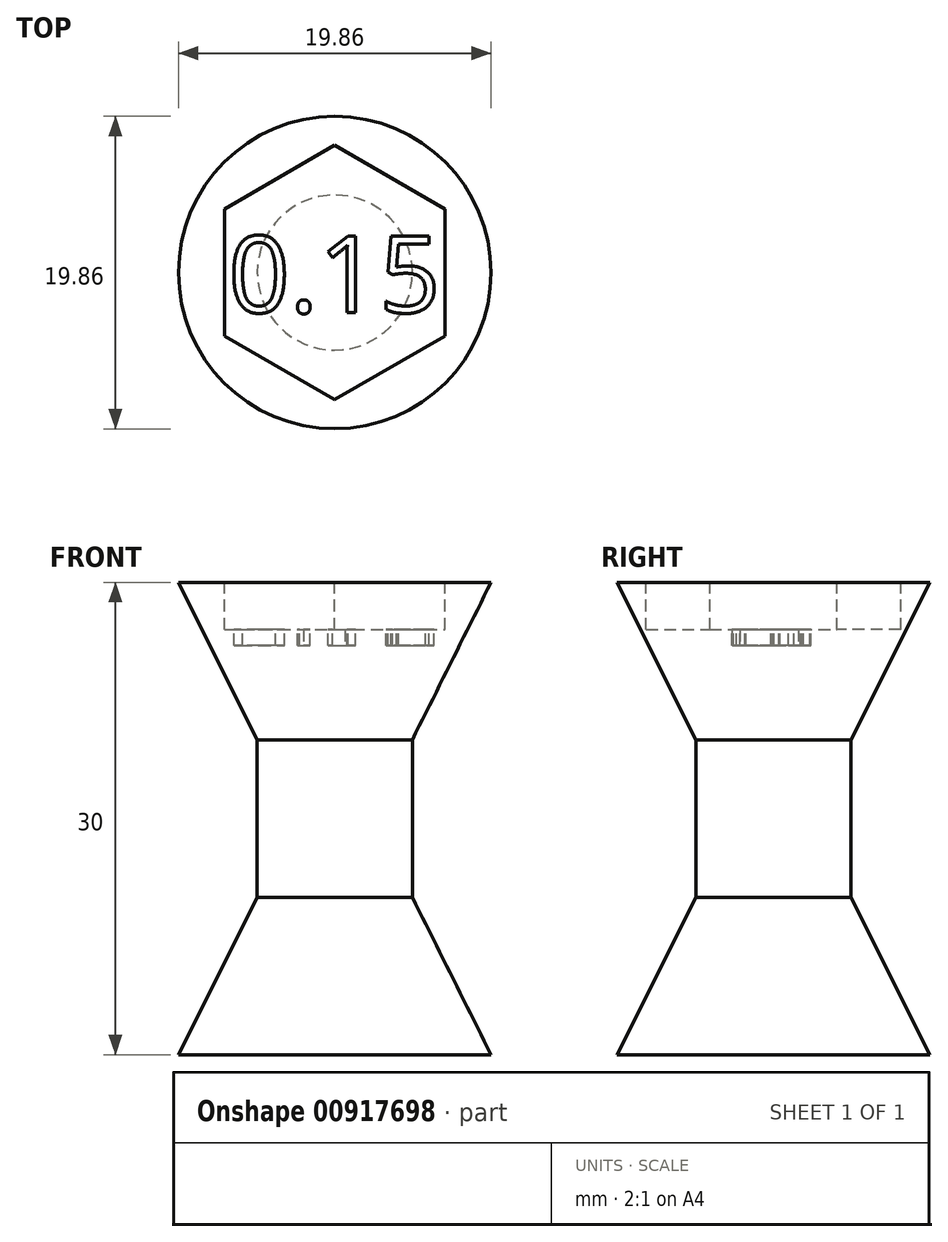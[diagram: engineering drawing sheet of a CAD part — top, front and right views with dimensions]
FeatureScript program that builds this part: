
annotation { "Feature Type Name" : "Feature", "Feature Type Description" : "" }
export const myFeature = defineFeature(function(context is Context, id is Id, definition is map)
    precondition{}
    {
        {
            var Q0;
            Q0=qCreatedBy(makeId("Front.planeOp"),FACE);
            var sketch = newSketch(context, id + "F0", { "sketchPlane" : qUnion([Q0])});
            skLineSegment(sketch, "E0", {"start": v(0, 15) * mm, "end": v(0, -15) * mm});
            skLineSegment(sketch, "E1", {"start": v(0, -15) * mm, "end": v(9.93, -15) * mm});
            skLineSegment(sketch, "E2", {"start": v(9.93, -15) * mm, "end": v(4.92, -5) * mm});
            skLineSegment(sketch, "E3", {"start": v(4.92, -5) * mm, "end": v(4.92, 5) * mm});
            skLineSegment(sketch, "E4", {"start": v(4.92, 5) * mm, "end": v(9.92, 15) * mm});
            skLineSegment(sketch, "E5", {"start": v(9.92, 15) * mm, "end": v(0, 15) * mm});
            skSolve(sketch);
        }
        {
            var Q0;
            Q0=makeQuery(id+"F0.imprint","IMPRINT",FACE,{"disambiguationData":[TD([[makeQuery(id+"F0.imprint","IMPRINT",EDGE,{"derivedFrom":sQuery(id+"F0.wireOp",EDGE,"E0")}),1.0]])]});
            var Q1;
            Q1=sQuery(id+"F0.wireOp",EDGE,"E0");
            var Q2;
            Q2=sQuery(id+"F0.wireOp",EDGE,"E1");
            var Q3;
            Q3=sQuery(id+"F0.wireOp",EDGE,"E2");
            var Q4;
            Q4=sQuery(id+"F0.wireOp",EDGE,"E3");
            var Q5;
            Q5=sQuery(id+"F0.wireOp",EDGE,"E4");
            var Q6;
            Q6=sQuery(id+"F0.wireOp",EDGE,"E5");
            var Q7;
            Q7=sQuery(id+"F0.wireOp",EDGE,"E0");
            revolve(context, id + "F1", {"surfaceOperationType" : NewSurfaceOperationType.ADD, "entities" : qUnion([Q0]), "surfaceEntities" : qUnion([Q1, Q2, Q3, Q4, Q5, Q6]), "axis" : qUnion([Q7]), "revolveType" : RevolveType.FULL});
        }
        {
            var Q0;
            Q0=makeQuery(id+"F1.opRevolve","SWEPT_FACE",FACE,{"disambiguationData":[OSD([sQuery(id+"F0.wireOp",EDGE,"E5")])]});
            var sketch = newSketch(context, id + "F2", { "sketchPlane" : qUnion([Q0])});
            skCircle(sketch, "E6.cCircle", {"center": v(0, 0) * mm, "radius": 7 * mm, "construction": true});
            skLineSegment(sketch, "E6.0", {"start": v(0, 8.08) * mm, "end": v(7, 4.04) * mm});
            skLineSegment(sketch, "E6.1", {"start": v(7, 4.04) * mm, "end": v(7, -4.04) * mm});
            skLineSegment(sketch, "E6.2", {"start": v(7, -4.04) * mm, "end": v(0, -8.08) * mm});
            skLineSegment(sketch, "E6.3", {"start": v(0, -8.08) * mm, "end": v(-7, -4.04) * mm});
            skLineSegment(sketch, "E6.4", {"start": v(-7, -4.04) * mm, "end": v(-7, 4.04) * mm});
            skLineSegment(sketch, "E6.5", {"start": v(-7, 4.04) * mm, "end": v(0, 8.08) * mm});
            skPoint(sketch, "E6.0.midPoint", {"position": v(3.5, 6.06) * mm});
            skSolve(sketch);
        }
        {
            var Q0;
            Q0 = qSketchRegion(id + "F2", true);
            extrude(context, id + "F3", {"entities" : qUnion([Q0]), "operationType" : NewBodyOperationType.REMOVE, "oppositeDirection" : true, "depth" : 3 * mm, "offsetDistance" : 25 * mm});
        }
        {
            var Q0;
            Q0=makeQuery(id+"F3.boolean.opBoolean","COPY",FACE,{"derivedFrom":makeQuery(id+"F3.opExtrude","CAP_FACE",FACE,{"disambiguationData":[OSD([sQuery(id+"F2.wireOp",EDGE,"E6.0"),sQuery(id+"F2.wireOp",EDGE,"E6.1"),sQuery(id+"F2.wireOp",EDGE,"E6.2"),sQuery(id+"F2.wireOp",EDGE,"E6.3"),sQuery(id+"F2.wireOp",EDGE,"E6.4"),sQuery(id+"F2.wireOp",EDGE,"E6.5")])],"isStart":false})});
            var sketch = newSketch(context, id + "F4", { "sketchPlane" : qUnion([Q0])});
            skText(sketch, "E7", { "text": "0.15", "fontName": "OpenSans-Regular.ttf"});
            const initialGuessF4  = {"E7": [-0.00675, -0.00254, 1, 0, 0.00489]};
            skSetInitialGuess(sketch, initialGuessF4);
            skSolve(sketch);
        }
        {
            var Q0;
            Q0 = qSketchRegion(id + "F4", true);
            extrude(context, id + "F5", {"entities" : qUnion([Q0]), "operationType" : NewBodyOperationType.REMOVE, "oppositeDirection" : true, "depth" : 1 * mm, "offsetDistance" : 25 * mm});
        }
    });
